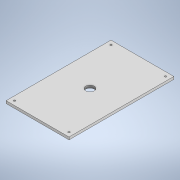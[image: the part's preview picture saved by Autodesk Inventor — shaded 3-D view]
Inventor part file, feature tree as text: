
AUTODESK INVENTOR PART (.ipt)
format: ipt  version: 2020 (Build 240168000, 168)  size: 110,080 bytes
history: native  units: mm
features: extrude x1, sketch x1
ambient origin geometry x8: Origin, YZ Plane, XZ Plane, XY Plane, X Axis, Y Axis, Z Axis, Center Point
bodies: Solide1 (feature_tree)
feature tree (2):
  extrude  "Extrusion1"  Depth=150.0mm
  sketch  "Esquisse1"
